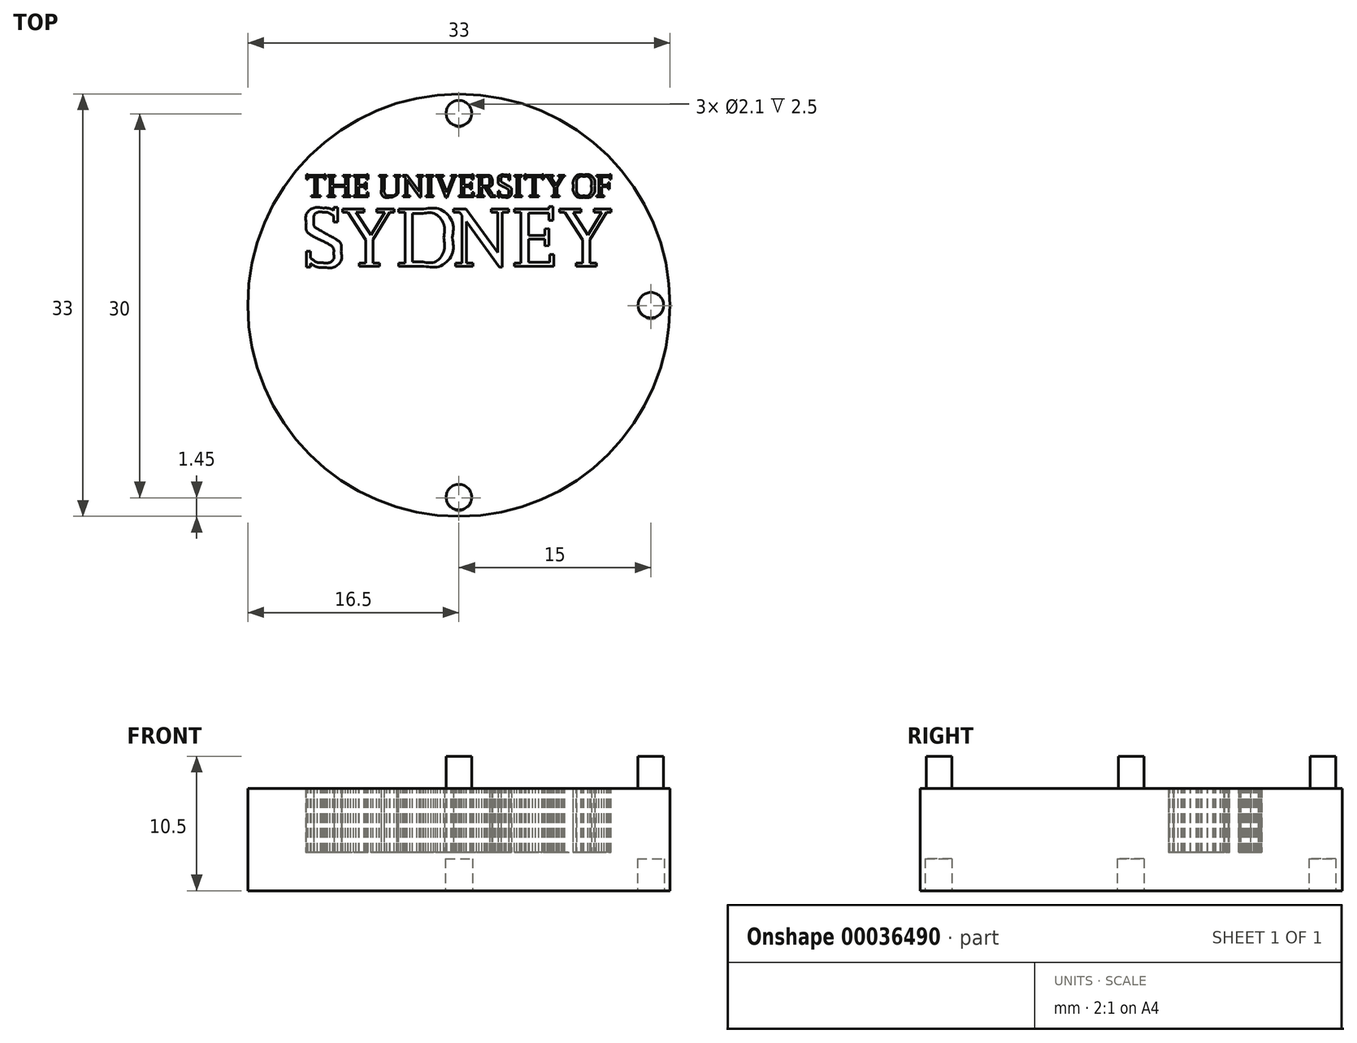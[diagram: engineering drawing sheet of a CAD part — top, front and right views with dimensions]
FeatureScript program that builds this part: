
annotation { "Feature Type Name" : "Feature", "Feature Type Description" : "" }
export const myFeature = defineFeature(function(context is Context, id is Id, definition is map)
    precondition{}
    {
        {
            var Q0;
            Q0=qCreatedBy(makeId("Top.planeOp"),FACE);
            var sketch = newSketch(context, id + "F0", { "sketchPlane" : qUnion([Q0])});
            skCircle(sketch, "E0", {"center": v(0, 0) * mm, "radius": 16.5 * mm});
            skSolve(sketch);
        }
        {
            var Q0;
            Q0=qSketchRegion(id+"F0",true);
            extrude(context, id + "F1", {"entities" : qUnion([Q0]), "depth" : 8 * mm});
        }
        {
            var Q0;
            Q0=makeQuery(id+"F1.opExtrude","CAP_FACE",FACE,{"disambiguationData":[OSD([sQuery(id+"F0.wireOp",EDGE,"E0")])],"isStart":true});
            var sketch = newSketch(context, id + "F2", { "sketchPlane" : qUnion([Q0])});
            skCircle(sketch, "E1", {"center": v(0, 15.05) * mm, "radius": 1.05 * mm});
            skCircle(sketch, "E2.1.0", {"center": v(15, 0.05) * mm, "radius": 1.05 * mm});
            skCircle(sketch, "E2.2.0", {"center": v(0, -14.95) * mm, "radius": 1.05 * mm});
            skPoint(sketch, "E2.center", {"position": v(0, 0.05) * mm});
            skLineSegment(sketch, "E2.anchor1", {"start": v(0, 0.05) * mm, "end": v(0, 15.05) * mm, "construction": true});
            skLineSegment(sketch, "E2.anchor2", {"start": v(0, 0.05) * mm, "end": v(0, -14.95) * mm, "construction": true});
            skSolve(sketch);
        }
        {
            var Q0;
            Q0=qSketchRegion(id+"F2",true);
            extrude(context, id + "F3", {"entities" : qUnion([Q0]), "operationType" : NewBodyOperationType.REMOVE, "oppositeDirection" : true, "depth" : 2.5 * mm});
        }
        {
            var Q0;
            Q0=makeQuery(id+"F1.opExtrude","CAP_FACE",FACE,{"disambiguationData":[OSD([sQuery(id+"F0.wireOp",EDGE,"E0")])],"isStart":false});
            var sketch = newSketch(context, id + "F4", { "sketchPlane" : qUnion([Q0])});
            skCircle(sketch, "E3", {"center": v(0, 15) * mm, "radius": 1 * mm});
            skCircle(sketch, "E4.1.0", {"center": v(15, 0) * mm, "radius": 1 * mm});
            skCircle(sketch, "E4.2.0", {"center": v(0, -15) * mm, "radius": 1 * mm});
            skPoint(sketch, "E4.center", {"position": v(0, 0) * mm});
            skLineSegment(sketch, "E4.anchor1", {"start": v(0, 0) * mm, "end": v(0, 15) * mm, "construction": true});
            skLineSegment(sketch, "E4.anchor2", {"start": v(0, 0) * mm, "end": v(0, -15) * mm, "construction": true});
            skSolve(sketch);
        }
        {
            var Q0;
            Q0=qSketchRegion(id+"F4",true);
            extrude(context, id + "F5", {"entities" : qUnion([Q0]), "operationType" : NewBodyOperationType.ADD, "depth" : 2.5 * mm});
        }
        {
            var Q0;
            Q0=makeQuery(id+"F1.opExtrude","CAP_FACE",FACE,{"disambiguationData":[OSD([sQuery(id+"F0.wireOp",EDGE,"E0")])],"isStart":false});
            var sketch = newSketch(context, id + "F6", { "sketchPlane" : qUnion([Q0])});
            skLineSegment(sketch, "E5", {"start": v(-10.8, 8.46) * mm, "end": v(-11.53, 8.46) * mm});
            skLineSegment(sketch, "E6", {"start": v(-11.53, 8.46) * mm, "end": v(-11.53, 8.56) * mm});
            skLineSegment(sketch, "E7", {"start": v(-11.53, 8.56) * mm, "end": v(-11.28, 8.56) * mm});
            skLineSegment(sketch, "E8", {"start": v(-11.28, 8.56) * mm, "end": v(-11.28, 10.03) * mm});
            skLineSegment(sketch, "E9", {"start": v(-11.28, 10.03) * mm, "end": v(-11.8, 10.03) * mm});
            skLineSegment(sketch, "E10", {"start": v(-11.8, 10.03) * mm, "end": v(-11.8, 9.82) * mm});
            skLineSegment(sketch, "E11", {"start": v(-11.8, 9.82) * mm, "end": v(-11.91, 9.82) * mm});
            skLineSegment(sketch, "E12", {"start": v(-11.91, 9.82) * mm, "end": v(-11.91, 10.23) * mm});
            skLineSegment(sketch, "E13", {"start": v(-11.91, 10.23) * mm, "end": v(-11.8, 10.23) * mm});
            skLineSegment(sketch, "E14", {"start": v(-11.8, 10.23) * mm, "end": v(-11.8, 10.15) * mm});
            skLineSegment(sketch, "E15", {"start": v(-11.8, 10.15) * mm, "end": v(-10.54, 10.15) * mm});
            skLineSegment(sketch, "E16", {"start": v(-10.54, 10.15) * mm, "end": v(-10.54, 10.23) * mm});
            skLineSegment(sketch, "E17", {"start": v(-10.54, 10.23) * mm, "end": v(-10.42, 10.23) * mm});
            skLineSegment(sketch, "E18", {"start": v(-10.42, 10.23) * mm, "end": v(-10.42, 9.82) * mm});
            skLineSegment(sketch, "E19", {"start": v(-10.42, 9.82) * mm, "end": v(-10.54, 9.82) * mm});
            skLineSegment(sketch, "E20", {"start": v(-10.54, 9.82) * mm, "end": v(-10.54, 10.03) * mm});
            skLineSegment(sketch, "E21", {"start": v(-10.54, 10.03) * mm, "end": v(-11.05, 10.03) * mm});
            skLineSegment(sketch, "E22", {"start": v(-11.05, 10.03) * mm, "end": v(-11.05, 8.56) * mm});
            skLineSegment(sketch, "E23", {"start": v(-11.05, 8.56) * mm, "end": v(-10.8, 8.56) * mm});
            skLineSegment(sketch, "E24", {"start": v(-10.8, 8.56) * mm, "end": v(-10.8, 8.46) * mm});
            skLineSegment(sketch, "E25", {"start": v(-8.47, 8.46) * mm, "end": v(-9.08, 8.46) * mm});
            skLineSegment(sketch, "E26", {"start": v(-9.08, 8.46) * mm, "end": v(-9.08, 8.56) * mm});
            skLineSegment(sketch, "E27", {"start": v(-9.08, 8.56) * mm, "end": v(-8.88, 8.56) * mm});
            skLineSegment(sketch, "E28", {"start": v(-8.88, 8.56) * mm, "end": v(-8.88, 9.26) * mm});
            skLineSegment(sketch, "E29", {"start": v(-8.88, 9.26) * mm, "end": v(-9.84, 9.26) * mm});
            skLineSegment(sketch, "E30", {"start": v(-9.84, 9.26) * mm, "end": v(-9.84, 8.56) * mm});
            skLineSegment(sketch, "E31", {"start": v(-9.84, 8.56) * mm, "end": v(-9.65, 8.56) * mm});
            skLineSegment(sketch, "E32", {"start": v(-9.65, 8.56) * mm, "end": v(-9.65, 8.46) * mm});
            skLineSegment(sketch, "E33", {"start": v(-9.65, 8.46) * mm, "end": v(-10.26, 8.46) * mm});
            skLineSegment(sketch, "E34", {"start": v(-10.26, 8.46) * mm, "end": v(-10.26, 8.56) * mm});
            skLineSegment(sketch, "E35", {"start": v(-10.26, 8.56) * mm, "end": v(-10.07, 8.56) * mm});
            skLineSegment(sketch, "E36", {"start": v(-10.07, 8.56) * mm, "end": v(-10.07, 10.06) * mm});
            skLineSegment(sketch, "E37", {"start": v(-10.07, 10.06) * mm, "end": v(-10.26, 10.06) * mm});
            skLineSegment(sketch, "E38", {"start": v(-10.26, 10.06) * mm, "end": v(-10.26, 10.15) * mm});
            skLineSegment(sketch, "E39", {"start": v(-10.26, 10.15) * mm, "end": v(-9.65, 10.15) * mm});
            skLineSegment(sketch, "E40", {"start": v(-9.65, 10.15) * mm, "end": v(-9.65, 10.06) * mm});
            skLineSegment(sketch, "E41", {"start": v(-9.65, 10.06) * mm, "end": v(-9.84, 10.06) * mm});
            skLineSegment(sketch, "E42", {"start": v(-9.84, 10.06) * mm, "end": v(-9.84, 9.38) * mm});
            skLineSegment(sketch, "E43", {"start": v(-9.84, 9.38) * mm, "end": v(-8.88, 9.38) * mm});
            skLineSegment(sketch, "E44", {"start": v(-8.88, 9.38) * mm, "end": v(-8.88, 10.06) * mm});
            skLineSegment(sketch, "E45", {"start": v(-8.88, 10.06) * mm, "end": v(-9.08, 10.06) * mm});
            skLineSegment(sketch, "E46", {"start": v(-9.08, 10.06) * mm, "end": v(-9.08, 10.15) * mm});
            skLineSegment(sketch, "E47", {"start": v(-9.08, 10.15) * mm, "end": v(-8.47, 10.15) * mm});
            skLineSegment(sketch, "E48", {"start": v(-8.47, 10.15) * mm, "end": v(-8.47, 10.06) * mm});
            skLineSegment(sketch, "E49", {"start": v(-8.47, 10.06) * mm, "end": v(-8.66, 10.06) * mm});
            skLineSegment(sketch, "E50", {"start": v(-8.66, 10.06) * mm, "end": v(-8.66, 8.56) * mm});
            skLineSegment(sketch, "E51", {"start": v(-8.66, 8.56) * mm, "end": v(-8.47, 8.56) * mm});
            skLineSegment(sketch, "E52", {"start": v(-8.47, 8.56) * mm, "end": v(-8.47, 8.46) * mm});
            skLineSegment(sketch, "E53", {"start": v(-7.08, 8.46) * mm, "end": v(-8.25, 8.46) * mm});
            skLineSegment(sketch, "E54", {"start": v(-8.25, 8.46) * mm, "end": v(-8.25, 8.56) * mm});
            skLineSegment(sketch, "E55", {"start": v(-8.25, 8.56) * mm, "end": v(-8.06, 8.56) * mm});
            skLineSegment(sketch, "E56", {"start": v(-8.06, 8.56) * mm, "end": v(-8.06, 10.06) * mm});
            skLineSegment(sketch, "E57", {"start": v(-8.06, 10.06) * mm, "end": v(-8.25, 10.06) * mm});
            skLineSegment(sketch, "E58", {"start": v(-8.25, 10.06) * mm, "end": v(-8.25, 10.15) * mm});
            skLineSegment(sketch, "E59", {"start": v(-8.25, 10.15) * mm, "end": v(-7.23, 10.15) * mm});
            skLineSegment(sketch, "E60", {"start": v(-7.23, 10.15) * mm, "end": v(-7.23, 10.23) * mm});
            skLineSegment(sketch, "E61", {"start": v(-7.23, 10.23) * mm, "end": v(-7.1, 10.23) * mm});
            skLineSegment(sketch, "E62", {"start": v(-7.1, 10.23) * mm, "end": v(-7.1, 9.82) * mm});
            skLineSegment(sketch, "E63", {"start": v(-7.1, 9.82) * mm, "end": v(-7.22, 9.82) * mm});
            skLineSegment(sketch, "E64", {"start": v(-7.22, 9.82) * mm, "end": v(-7.22, 10.04) * mm});
            skLineSegment(sketch, "E65", {"start": v(-7.22, 10.04) * mm, "end": v(-7.83, 10.04) * mm});
            skLineSegment(sketch, "E66", {"start": v(-7.83, 10.04) * mm, "end": v(-7.83, 9.38) * mm});
            skLineSegment(sketch, "E67", {"start": v(-7.83, 9.38) * mm, "end": v(-7.35, 9.38) * mm});
            skLineSegment(sketch, "E68", {"start": v(-7.35, 9.38) * mm, "end": v(-7.35, 9.57) * mm});
            skLineSegment(sketch, "E69", {"start": v(-7.35, 9.57) * mm, "end": v(-7.23, 9.57) * mm});
            skLineSegment(sketch, "E70", {"start": v(-7.23, 9.57) * mm, "end": v(-7.23, 9.07) * mm});
            skLineSegment(sketch, "E71", {"start": v(-7.23, 9.07) * mm, "end": v(-7.35, 9.07) * mm});
            skLineSegment(sketch, "E72", {"start": v(-7.35, 9.07) * mm, "end": v(-7.35, 9.26) * mm});
            skLineSegment(sketch, "E73", {"start": v(-7.35, 9.26) * mm, "end": v(-7.83, 9.26) * mm});
            skLineSegment(sketch, "E74", {"start": v(-7.83, 9.26) * mm, "end": v(-7.83, 8.58) * mm});
            skLineSegment(sketch, "E75", {"start": v(-7.83, 8.58) * mm, "end": v(-7.2, 8.58) * mm});
            skLineSegment(sketch, "E76", {"start": v(-7.2, 8.58) * mm, "end": v(-7.2, 8.8) * mm});
            skLineSegment(sketch, "E77", {"start": v(-7.2, 8.8) * mm, "end": v(-7.08, 8.8) * mm});
            skLineSegment(sketch, "E78", {"start": v(-7.08, 8.8) * mm, "end": v(-7.08, 8.46) * mm});
            skLineSegment(sketch, "E79", {"start": v(-4.55, 10.06) * mm, "end": v(-4.74, 10.06) * mm});
            skLineSegment(sketch, "E80", {"start": v(-4.74, 10.06) * mm, "end": v(-4.74, 9.08) * mm});
            skFitSpline(sketch, "E81", {"points": [v(-4.74, 9.08) * mm, v(-4.74, 8.8) * mm, v(-4.84, 8.63) * mm, v(-5.05, 8.52) * mm]});
            skFitSpline(sketch, "E82", {"points": [v(-5.05, 8.52) * mm, v(-5.16, 8.46) * mm, v(-5.28, 8.43) * mm, v(-5.4, 8.43) * mm]});
            skFitSpline(sketch, "E83", {"points": [v(-5.4, 8.43) * mm, v(-5.78, 8.43) * mm, v(-6.06, 8.67) * mm, v(-6.06, 9.01) * mm]});
            skLineSegment(sketch, "E84", {"start": v(-6.06, 9.01) * mm, "end": v(-6.06, 10.06) * mm});
            skLineSegment(sketch, "E85", {"start": v(-6.06, 10.06) * mm, "end": v(-6.25, 10.06) * mm});
            skLineSegment(sketch, "E86", {"start": v(-6.25, 10.06) * mm, "end": v(-6.25, 10.15) * mm});
            skLineSegment(sketch, "E87", {"start": v(-6.25, 10.15) * mm, "end": v(-5.64, 10.15) * mm});
            skLineSegment(sketch, "E88", {"start": v(-5.64, 10.15) * mm, "end": v(-5.64, 10.06) * mm});
            skLineSegment(sketch, "E89", {"start": v(-5.64, 10.06) * mm, "end": v(-5.83, 10.06) * mm});
            skLineSegment(sketch, "E90", {"start": v(-5.83, 10.06) * mm, "end": v(-5.83, 9.09) * mm});
            skFitSpline(sketch, "E91", {"points": [v(-5.83, 9.09) * mm, v(-5.83, 8.78) * mm, v(-5.65, 8.58) * mm, v(-5.36, 8.58) * mm]});
            skFitSpline(sketch, "E92", {"points": [v(-5.36, 8.58) * mm, v(-5.07, 8.58) * mm, v(-4.87, 8.79) * mm, v(-4.87, 9.1) * mm]});
            skLineSegment(sketch, "E93", {"start": v(-4.87, 9.1) * mm, "end": v(-4.87, 10.06) * mm});
            skLineSegment(sketch, "E94", {"start": v(-4.87, 10.06) * mm, "end": v(-5.07, 10.06) * mm});
            skLineSegment(sketch, "E95", {"start": v(-5.07, 10.06) * mm, "end": v(-5.07, 10.15) * mm});
            skLineSegment(sketch, "E96", {"start": v(-5.07, 10.15) * mm, "end": v(-4.55, 10.15) * mm});
            skLineSegment(sketch, "E97", {"start": v(-4.55, 10.15) * mm, "end": v(-4.55, 10.06) * mm});
            skLineSegment(sketch, "E98", {"start": v(-2.97, 8.43) * mm, "end": v(-3.05, 8.43) * mm});
            skLineSegment(sketch, "E99", {"start": v(-3.05, 8.43) * mm, "end": v(-4.03, 9.79) * mm});
            skLineSegment(sketch, "E100", {"start": v(-4.03, 9.79) * mm, "end": v(-4.03, 8.56) * mm});
            skLineSegment(sketch, "E101", {"start": v(-4.03, 8.56) * mm, "end": v(-3.84, 8.56) * mm});
            skLineSegment(sketch, "E102", {"start": v(-3.84, 8.56) * mm, "end": v(-3.84, 8.46) * mm});
            skLineSegment(sketch, "E103", {"start": v(-3.84, 8.46) * mm, "end": v(-4.36, 8.46) * mm});
            skLineSegment(sketch, "E104", {"start": v(-4.36, 8.46) * mm, "end": v(-4.36, 8.56) * mm});
            skLineSegment(sketch, "E105", {"start": v(-4.36, 8.56) * mm, "end": v(-4.16, 8.56) * mm});
            skLineSegment(sketch, "E106", {"start": v(-4.16, 8.56) * mm, "end": v(-4.16, 9.96) * mm});
            skLineSegment(sketch, "E107", {"start": v(-4.16, 9.96) * mm, "end": v(-4.23, 10.06) * mm});
            skLineSegment(sketch, "E108", {"start": v(-4.23, 10.06) * mm, "end": v(-4.4, 10.06) * mm});
            skLineSegment(sketch, "E109", {"start": v(-4.4, 10.06) * mm, "end": v(-4.4, 10.15) * mm});
            skLineSegment(sketch, "E110", {"start": v(-4.4, 10.15) * mm, "end": v(-4.04, 10.15) * mm});
            skLineSegment(sketch, "E111", {"start": v(-4.04, 10.15) * mm, "end": v(-3.1, 8.87) * mm});
            skLineSegment(sketch, "E112", {"start": v(-3.1, 8.87) * mm, "end": v(-3.1, 10.06) * mm});
            skLineSegment(sketch, "E113", {"start": v(-3.1, 10.06) * mm, "end": v(-3.3, 10.06) * mm});
            skLineSegment(sketch, "E114", {"start": v(-3.3, 10.06) * mm, "end": v(-3.3, 10.15) * mm});
            skLineSegment(sketch, "E115", {"start": v(-3.3, 10.15) * mm, "end": v(-2.78, 10.15) * mm});
            skLineSegment(sketch, "E116", {"start": v(-2.78, 10.15) * mm, "end": v(-2.78, 10.06) * mm});
            skLineSegment(sketch, "E117", {"start": v(-2.78, 10.06) * mm, "end": v(-2.97, 10.06) * mm});
            skLineSegment(sketch, "E118", {"start": v(-2.97, 10.06) * mm, "end": v(-2.97, 8.43) * mm});
            skLineSegment(sketch, "E119", {"start": v(-1.98, 8.46) * mm, "end": v(-2.6, 8.46) * mm});
            skLineSegment(sketch, "E120", {"start": v(-2.6, 8.46) * mm, "end": v(-2.6, 8.56) * mm});
            skLineSegment(sketch, "E121", {"start": v(-2.6, 8.56) * mm, "end": v(-2.4, 8.56) * mm});
            skLineSegment(sketch, "E122", {"start": v(-2.4, 8.56) * mm, "end": v(-2.4, 10.06) * mm});
            skLineSegment(sketch, "E123", {"start": v(-2.4, 10.06) * mm, "end": v(-2.6, 10.06) * mm});
            skLineSegment(sketch, "E124", {"start": v(-2.6, 10.06) * mm, "end": v(-2.6, 10.15) * mm});
            skLineSegment(sketch, "E125", {"start": v(-2.6, 10.15) * mm, "end": v(-1.98, 10.15) * mm});
            skLineSegment(sketch, "E126", {"start": v(-1.98, 10.15) * mm, "end": v(-1.98, 10.06) * mm});
            skLineSegment(sketch, "E127", {"start": v(-1.98, 10.06) * mm, "end": v(-2.17, 10.06) * mm});
            skLineSegment(sketch, "E128", {"start": v(-2.17, 10.06) * mm, "end": v(-2.17, 8.56) * mm});
            skLineSegment(sketch, "E129", {"start": v(-2.17, 8.56) * mm, "end": v(-1.98, 8.56) * mm});
            skLineSegment(sketch, "E130", {"start": v(-1.98, 8.56) * mm, "end": v(-1.98, 8.46) * mm});
            skLineSegment(sketch, "E131", {"start": v(-0.94, 8.42) * mm, "end": v(-1.03, 8.42) * mm});
            skLineSegment(sketch, "E132", {"start": v(-1.03, 8.42) * mm, "end": v(-1.68, 10.06) * mm});
            skLineSegment(sketch, "E133", {"start": v(-1.68, 10.06) * mm, "end": v(-1.83, 10.06) * mm});
            skLineSegment(sketch, "E134", {"start": v(-1.83, 10.06) * mm, "end": v(-1.83, 10.15) * mm});
            skLineSegment(sketch, "E135", {"start": v(-1.83, 10.15) * mm, "end": v(-1.2, 10.15) * mm});
            skLineSegment(sketch, "E136", {"start": v(-1.2, 10.15) * mm, "end": v(-1.2, 10.06) * mm});
            skLineSegment(sketch, "E137", {"start": v(-1.2, 10.06) * mm, "end": v(-1.43, 10.06) * mm});
            skLineSegment(sketch, "E138", {"start": v(-1.43, 10.06) * mm, "end": v(-0.94, 8.8) * mm});
            skLineSegment(sketch, "E139", {"start": v(-0.94, 8.8) * mm, "end": v(-0.44, 10.06) * mm});
            skLineSegment(sketch, "E140", {"start": v(-0.44, 10.06) * mm, "end": v(-0.61, 10.06) * mm});
            skLineSegment(sketch, "E141", {"start": v(-0.61, 10.06) * mm, "end": v(-0.61, 10.15) * mm});
            skLineSegment(sketch, "E142", {"start": v(-0.61, 10.15) * mm, "end": v(-0.18, 10.15) * mm});
            skLineSegment(sketch, "E143", {"start": v(-0.18, 10.15) * mm, "end": v(-0.18, 10.06) * mm});
            skLineSegment(sketch, "E144", {"start": v(-0.18, 10.06) * mm, "end": v(-0.3, 10.06) * mm});
            skLineSegment(sketch, "E145", {"start": v(-0.3, 10.06) * mm, "end": v(-0.94, 8.42) * mm});
            skLineSegment(sketch, "E146", {"start": v(1.15, 8.46) * mm, "end": v(-0.02, 8.46) * mm});
            skLineSegment(sketch, "E147", {"start": v(-0.02, 8.46) * mm, "end": v(-0.02, 8.56) * mm});
            skLineSegment(sketch, "E148", {"start": v(-0.02, 8.56) * mm, "end": v(0.17, 8.56) * mm});
            skLineSegment(sketch, "E149", {"start": v(0.17, 8.56) * mm, "end": v(0.17, 10.06) * mm});
            skLineSegment(sketch, "E150", {"start": v(0.17, 10.06) * mm, "end": v(-0.02, 10.06) * mm});
            skLineSegment(sketch, "E151", {"start": v(-0.02, 10.06) * mm, "end": v(-0.02, 10.15) * mm});
            skLineSegment(sketch, "E152", {"start": v(-0.02, 10.15) * mm, "end": v(1, 10.15) * mm});
            skLineSegment(sketch, "E153", {"start": v(1, 10.15) * mm, "end": v(1, 10.23) * mm});
            skLineSegment(sketch, "E154", {"start": v(1, 10.23) * mm, "end": v(1.12, 10.23) * mm});
            skLineSegment(sketch, "E155", {"start": v(1.12, 10.23) * mm, "end": v(1.12, 9.82) * mm});
            skLineSegment(sketch, "E156", {"start": v(1.12, 9.82) * mm, "end": v(1, 9.82) * mm});
            skLineSegment(sketch, "E157", {"start": v(1, 9.82) * mm, "end": v(1, 10.04) * mm});
            skLineSegment(sketch, "E158", {"start": v(1, 10.04) * mm, "end": v(0.4, 10.04) * mm});
            skLineSegment(sketch, "E159", {"start": v(0.4, 10.04) * mm, "end": v(0.4, 9.38) * mm});
            skLineSegment(sketch, "E160", {"start": v(0.4, 9.38) * mm, "end": v(0.88, 9.38) * mm});
            skLineSegment(sketch, "E161", {"start": v(0.88, 9.38) * mm, "end": v(0.88, 9.57) * mm});
            skLineSegment(sketch, "E162", {"start": v(0.88, 9.57) * mm, "end": v(1, 9.57) * mm});
            skLineSegment(sketch, "E163", {"start": v(1, 9.57) * mm, "end": v(1, 9.07) * mm});
            skLineSegment(sketch, "E164", {"start": v(1, 9.07) * mm, "end": v(0.88, 9.07) * mm});
            skLineSegment(sketch, "E165", {"start": v(0.88, 9.07) * mm, "end": v(0.88, 9.26) * mm});
            skLineSegment(sketch, "E166", {"start": v(0.88, 9.26) * mm, "end": v(0.4, 9.26) * mm});
            skLineSegment(sketch, "E167", {"start": v(0.4, 9.26) * mm, "end": v(0.4, 8.58) * mm});
            skLineSegment(sketch, "E168", {"start": v(0.4, 8.58) * mm, "end": v(1.03, 8.58) * mm});
            skLineSegment(sketch, "E169", {"start": v(1.03, 8.58) * mm, "end": v(1.03, 8.8) * mm});
            skLineSegment(sketch, "E170", {"start": v(1.03, 8.8) * mm, "end": v(1.15, 8.8) * mm});
            skLineSegment(sketch, "E171", {"start": v(1.15, 8.8) * mm, "end": v(1.15, 8.46) * mm});
            skLineSegment(sketch, "E172", {"start": v(1.8, 9.34) * mm, "end": v(2.06, 9.34) * mm});
            skFitSpline(sketch, "E173", {"points": [v(2.06, 9.34) * mm, v(2.25, 9.34) * mm, v(2.39, 9.48) * mm, v(2.39, 9.7) * mm]});
            skFitSpline(sketch, "E174", {"points": [v(2.39, 9.7) * mm, v(2.39, 9.91) * mm, v(2.27, 10.04) * mm, v(2.05, 10.04) * mm]});
            skLineSegment(sketch, "E175", {"start": v(2.05, 10.04) * mm, "end": v(1.8, 10.04) * mm});
            skLineSegment(sketch, "E176", {"start": v(1.8, 10.04) * mm, "end": v(1.8, 9.34) * mm});
            skLineSegment(sketch, "E177", {"start": v(2.87, 8.46) * mm, "end": v(2.66, 8.46) * mm});
            skFitSpline(sketch, "E178", {"points": [v(2.66, 8.46) * mm, v(2.5, 8.46) * mm, v(2.48, 8.48) * mm, v(2.4, 8.61) * mm]});
            skLineSegment(sketch, "E179", {"start": v(2.4, 8.61) * mm, "end": v(2, 9.22) * mm});
            skLineSegment(sketch, "E180", {"start": v(2, 9.22) * mm, "end": v(1.8, 9.22) * mm});
            skLineSegment(sketch, "E181", {"start": v(1.8, 9.22) * mm, "end": v(1.8, 8.56) * mm});
            skLineSegment(sketch, "E182", {"start": v(1.8, 8.56) * mm, "end": v(2, 8.56) * mm});
            skLineSegment(sketch, "E183", {"start": v(2, 8.56) * mm, "end": v(2, 8.46) * mm});
            skLineSegment(sketch, "E184", {"start": v(2, 8.46) * mm, "end": v(1.4, 8.46) * mm});
            skLineSegment(sketch, "E185", {"start": v(1.4, 8.46) * mm, "end": v(1.4, 8.56) * mm});
            skLineSegment(sketch, "E186", {"start": v(1.4, 8.56) * mm, "end": v(1.58, 8.56) * mm});
            skLineSegment(sketch, "E187", {"start": v(1.58, 8.56) * mm, "end": v(1.58, 10.06) * mm});
            skLineSegment(sketch, "E188", {"start": v(1.58, 10.06) * mm, "end": v(1.4, 10.06) * mm});
            skLineSegment(sketch, "E189", {"start": v(1.4, 10.06) * mm, "end": v(1.4, 10.15) * mm});
            skLineSegment(sketch, "E190", {"start": v(1.4, 10.15) * mm, "end": v(2.1, 10.15) * mm});
            skFitSpline(sketch, "E191", {"points": [v(2.1, 10.15) * mm, v(2.35, 10.15) * mm, v(2.5, 10.08) * mm, v(2.57, 9.93) * mm]});
            skFitSpline(sketch, "E192", {"points": [v(2.57, 9.93) * mm, v(2.6, 9.86) * mm, v(2.62, 9.78) * mm, v(2.62, 9.7) * mm]});
            skFitSpline(sketch, "E193", {"points": [v(2.62, 9.7) * mm, v(2.62, 9.45) * mm, v(2.48, 9.3) * mm, v(2.24, 9.25) * mm]});
            skLineSegment(sketch, "E194", {"start": v(2.24, 9.25) * mm, "end": v(2.6, 8.69) * mm});
            skFitSpline(sketch, "E195", {"points": [v(2.6, 8.69) * mm, v(2.67, 8.6) * mm, v(2.7, 8.56) * mm, v(2.77, 8.56) * mm]});
            skLineSegment(sketch, "E196", {"start": v(2.77, 8.56) * mm, "end": v(2.87, 8.56) * mm});
            skLineSegment(sketch, "E197", {"start": v(2.87, 8.56) * mm, "end": v(2.87, 8.46) * mm});
            skLineSegment(sketch, "E198", {"start": v(3.2, 8.44) * mm, "end": v(3.08, 8.44) * mm});
            skLineSegment(sketch, "E199", {"start": v(3.08, 8.44) * mm, "end": v(3.08, 8.9) * mm});
            skLineSegment(sketch, "E200", {"start": v(3.08, 8.9) * mm, "end": v(3.2, 8.9) * mm});
            skLineSegment(sketch, "E201", {"start": v(3.2, 8.9) * mm, "end": v(3.2, 8.7) * mm});
            skFitSpline(sketch, "E202", {"points": [v(3.2, 8.7) * mm, v(3.36, 8.6) * mm, v(3.43, 8.57) * mm, v(3.54, 8.57) * mm]});
            skFitSpline(sketch, "E203", {"points": [v(3.54, 8.57) * mm, v(3.74, 8.57) * mm, v(3.88, 8.67) * mm, v(3.88, 8.84) * mm]});
            skFitSpline(sketch, "E204", {"points": [v(3.88, 8.84) * mm, v(3.88, 8.98) * mm, v(3.78, 9.09) * mm, v(3.5, 9.23) * mm]});
            skFitSpline(sketch, "E205", {"points": [v(3.5, 9.23) * mm, v(3.18, 9.4) * mm, v(3.07, 9.53) * mm, v(3.07, 9.74) * mm]});
            skFitSpline(sketch, "E206", {"points": [v(3.07, 9.74) * mm, v(3.07, 10) * mm, v(3.29, 10.19) * mm, v(3.58, 10.19) * mm]});
            skFitSpline(sketch, "E207", {"points": [v(3.58, 10.19) * mm, v(3.7, 10.19) * mm, v(3.8, 10.16) * mm, v(3.88, 10.11) * mm]});
            skLineSegment(sketch, "E208", {"start": v(3.88, 10.11) * mm, "end": v(3.88, 10.2) * mm});
            skLineSegment(sketch, "E209", {"start": v(3.88, 10.2) * mm, "end": v(4, 10.2) * mm});
            skLineSegment(sketch, "E210", {"start": v(4, 10.2) * mm, "end": v(4, 9.77) * mm});
            skLineSegment(sketch, "E211", {"start": v(4, 9.77) * mm, "end": v(3.88, 9.77) * mm});
            skLineSegment(sketch, "E212", {"start": v(3.88, 9.77) * mm, "end": v(3.88, 9.95) * mm});
            skFitSpline(sketch, "E213", {"points": [v(3.88, 9.95) * mm, v(3.75, 10.04) * mm, v(3.69, 10.06) * mm, v(3.59, 10.06) * mm]});
            skFitSpline(sketch, "E214", {"points": [v(3.59, 10.06) * mm, v(3.41, 10.06) * mm, v(3.3, 9.96) * mm, v(3.3, 9.8) * mm]});
            skFitSpline(sketch, "E215", {"points": [v(3.3, 9.8) * mm, v(3.3, 9.67) * mm, v(3.37, 9.6) * mm, v(3.7, 9.4) * mm]});
            skFitSpline(sketch, "E216", {"points": [v(3.7, 9.4) * mm, v(4.01, 9.22) * mm, v(4.1, 9.11) * mm, v(4.1, 8.9) * mm]});
            skFitSpline(sketch, "E217", {"points": [v(4.1, 8.9) * mm, v(4.1, 8.63) * mm, v(3.89, 8.43) * mm, v(3.6, 8.43) * mm]});
            skFitSpline(sketch, "E218", {"points": [v(3.6, 8.43) * mm, v(3.43, 8.43) * mm, v(3.33, 8.46) * mm, v(3.2, 8.54) * mm]});
            skLineSegment(sketch, "E219", {"start": v(3.2, 8.54) * mm, "end": v(3.2, 8.44) * mm});
            skLineSegment(sketch, "E220", {"start": v(4.95, 8.46) * mm, "end": v(4.34, 8.46) * mm});
            skLineSegment(sketch, "E221", {"start": v(4.34, 8.46) * mm, "end": v(4.34, 8.56) * mm});
            skLineSegment(sketch, "E222", {"start": v(4.34, 8.56) * mm, "end": v(4.53, 8.56) * mm});
            skLineSegment(sketch, "E223", {"start": v(4.53, 8.56) * mm, "end": v(4.53, 10.06) * mm});
            skLineSegment(sketch, "E224", {"start": v(4.53, 10.06) * mm, "end": v(4.34, 10.06) * mm});
            skLineSegment(sketch, "E225", {"start": v(4.34, 10.06) * mm, "end": v(4.34, 10.15) * mm});
            skLineSegment(sketch, "E226", {"start": v(4.34, 10.15) * mm, "end": v(4.95, 10.15) * mm});
            skLineSegment(sketch, "E227", {"start": v(4.95, 10.15) * mm, "end": v(4.95, 10.06) * mm});
            skLineSegment(sketch, "E228", {"start": v(4.95, 10.06) * mm, "end": v(4.76, 10.06) * mm});
            skLineSegment(sketch, "E229", {"start": v(4.76, 10.06) * mm, "end": v(4.76, 8.56) * mm});
            skLineSegment(sketch, "E230", {"start": v(4.76, 8.56) * mm, "end": v(4.95, 8.56) * mm});
            skLineSegment(sketch, "E231", {"start": v(4.95, 8.56) * mm, "end": v(4.95, 8.46) * mm});
            skLineSegment(sketch, "E232", {"start": v(6.24, 8.46) * mm, "end": v(5.5, 8.46) * mm});
            skLineSegment(sketch, "E233", {"start": v(5.5, 8.46) * mm, "end": v(5.5, 8.56) * mm});
            skLineSegment(sketch, "E234", {"start": v(5.5, 8.56) * mm, "end": v(5.75, 8.56) * mm});
            skLineSegment(sketch, "E235", {"start": v(5.75, 8.56) * mm, "end": v(5.75, 10.03) * mm});
            skLineSegment(sketch, "E236", {"start": v(5.75, 10.03) * mm, "end": v(5.24, 10.03) * mm});
            skLineSegment(sketch, "E237", {"start": v(5.24, 10.03) * mm, "end": v(5.24, 9.82) * mm});
            skLineSegment(sketch, "E238", {"start": v(5.24, 9.82) * mm, "end": v(5.12, 9.82) * mm});
            skLineSegment(sketch, "E239", {"start": v(5.12, 9.82) * mm, "end": v(5.12, 10.23) * mm});
            skLineSegment(sketch, "E240", {"start": v(5.12, 10.23) * mm, "end": v(5.24, 10.23) * mm});
            skLineSegment(sketch, "E241", {"start": v(5.24, 10.23) * mm, "end": v(5.24, 10.15) * mm});
            skLineSegment(sketch, "E242", {"start": v(5.24, 10.15) * mm, "end": v(6.5, 10.15) * mm});
            skLineSegment(sketch, "E243", {"start": v(6.5, 10.15) * mm, "end": v(6.5, 10.23) * mm});
            skLineSegment(sketch, "E244", {"start": v(6.5, 10.23) * mm, "end": v(6.62, 10.23) * mm});
            skLineSegment(sketch, "E245", {"start": v(6.62, 10.23) * mm, "end": v(6.62, 9.82) * mm});
            skLineSegment(sketch, "E246", {"start": v(6.62, 9.82) * mm, "end": v(6.5, 9.82) * mm});
            skLineSegment(sketch, "E247", {"start": v(6.5, 9.82) * mm, "end": v(6.5, 10.03) * mm});
            skLineSegment(sketch, "E248", {"start": v(6.5, 10.03) * mm, "end": v(5.98, 10.03) * mm});
            skLineSegment(sketch, "E249", {"start": v(5.98, 10.03) * mm, "end": v(5.98, 8.56) * mm});
            skLineSegment(sketch, "E250", {"start": v(5.98, 8.56) * mm, "end": v(6.24, 8.56) * mm});
            skLineSegment(sketch, "E251", {"start": v(6.24, 8.56) * mm, "end": v(6.24, 8.46) * mm});
            skLineSegment(sketch, "E252", {"start": v(7.86, 8.46) * mm, "end": v(7.25, 8.46) * mm});
            skLineSegment(sketch, "E253", {"start": v(7.25, 8.46) * mm, "end": v(7.25, 8.56) * mm});
            skLineSegment(sketch, "E254", {"start": v(7.25, 8.56) * mm, "end": v(7.44, 8.56) * mm});
            skLineSegment(sketch, "E255", {"start": v(7.44, 8.56) * mm, "end": v(7.44, 9.24) * mm});
            skLineSegment(sketch, "E256", {"start": v(7.44, 9.24) * mm, "end": v(6.9, 10.06) * mm});
            skLineSegment(sketch, "E257", {"start": v(6.9, 10.06) * mm, "end": v(6.76, 10.06) * mm});
            skLineSegment(sketch, "E258", {"start": v(6.76, 10.06) * mm, "end": v(6.76, 10.15) * mm});
            skLineSegment(sketch, "E259", {"start": v(6.76, 10.15) * mm, "end": v(7.4, 10.15) * mm});
            skLineSegment(sketch, "E260", {"start": v(7.4, 10.15) * mm, "end": v(7.4, 10.06) * mm});
            skLineSegment(sketch, "E261", {"start": v(7.4, 10.06) * mm, "end": v(7.16, 10.06) * mm});
            skLineSegment(sketch, "E262", {"start": v(7.16, 10.06) * mm, "end": v(7.6, 9.39) * mm});
            skLineSegment(sketch, "E263", {"start": v(7.6, 9.39) * mm, "end": v(8, 10.06) * mm});
            skLineSegment(sketch, "E264", {"start": v(8, 10.06) * mm, "end": v(7.77, 10.06) * mm});
            skLineSegment(sketch, "E265", {"start": v(7.77, 10.06) * mm, "end": v(7.77, 10.15) * mm});
            skLineSegment(sketch, "E266", {"start": v(7.77, 10.15) * mm, "end": v(8.29, 10.15) * mm});
            skLineSegment(sketch, "E267", {"start": v(8.29, 10.15) * mm, "end": v(8.29, 10.06) * mm});
            skLineSegment(sketch, "E268", {"start": v(8.29, 10.06) * mm, "end": v(8.15, 10.06) * mm});
            skLineSegment(sketch, "E269", {"start": v(8.15, 10.06) * mm, "end": v(7.66, 9.26) * mm});
            skLineSegment(sketch, "E270", {"start": v(7.66, 9.26) * mm, "end": v(7.66, 8.56) * mm});
            skLineSegment(sketch, "E271", {"start": v(7.66, 8.56) * mm, "end": v(7.86, 8.56) * mm});
            skLineSegment(sketch, "E272", {"start": v(7.86, 8.56) * mm, "end": v(7.86, 8.46) * mm});
            skFitSpline(sketch, "E273", {"points": [v(9.2, 9.3) * mm, v(9.2, 8.87) * mm, v(9.44, 8.56) * mm, v(9.78, 8.56) * mm]});
            skFitSpline(sketch, "E274", {"points": [v(9.78, 8.56) * mm, v(10.1, 8.56) * mm, v(10.34, 8.88) * mm, v(10.34, 9.3) * mm]});
            skFitSpline(sketch, "E275", {"points": [v(10.34, 9.3) * mm, v(10.34, 9.74) * mm, v(10.1, 10.05) * mm, v(9.78, 10.05) * mm]});
            skFitSpline(sketch, "E276", {"points": [v(9.78, 10.05) * mm, v(9.44, 10.05) * mm, v(9.2, 9.74) * mm, v(9.2, 9.3) * mm]});
            skFitSpline(sketch, "E277", {"points": [v(8.95, 9.3) * mm, v(8.95, 9.79) * mm, v(9.32, 10.19) * mm, v(9.78, 10.19) * mm]});
            skFitSpline(sketch, "E278", {"points": [v(9.78, 10.19) * mm, v(10.22, 10.19) * mm, v(10.6, 9.79) * mm, v(10.6, 9.3) * mm]});
            skFitSpline(sketch, "E279", {"points": [v(10.6, 9.3) * mm, v(10.6, 8.83) * mm, v(10.22, 8.43) * mm, v(9.78, 8.43) * mm]});
            skFitSpline(sketch, "E280", {"points": [v(9.78, 8.43) * mm, v(9.33, 8.43) * mm, v(8.95, 8.83) * mm, v(8.95, 9.3) * mm]});
            skLineSegment(sketch, "E281", {"start": v(11.37, 8.46) * mm, "end": v(10.76, 8.46) * mm});
            skLineSegment(sketch, "E282", {"start": v(10.76, 8.46) * mm, "end": v(10.76, 8.56) * mm});
            skLineSegment(sketch, "E283", {"start": v(10.76, 8.56) * mm, "end": v(10.95, 8.56) * mm});
            skLineSegment(sketch, "E284", {"start": v(10.95, 8.56) * mm, "end": v(10.95, 10.06) * mm});
            skLineSegment(sketch, "E285", {"start": v(10.95, 10.06) * mm, "end": v(10.76, 10.06) * mm});
            skLineSegment(sketch, "E286", {"start": v(10.76, 10.06) * mm, "end": v(10.76, 10.15) * mm});
            skLineSegment(sketch, "E287", {"start": v(10.76, 10.15) * mm, "end": v(11.78, 10.15) * mm});
            skLineSegment(sketch, "E288", {"start": v(11.78, 10.15) * mm, "end": v(11.78, 10.23) * mm});
            skLineSegment(sketch, "E289", {"start": v(11.78, 10.23) * mm, "end": v(11.9, 10.23) * mm});
            skLineSegment(sketch, "E290", {"start": v(11.9, 10.23) * mm, "end": v(11.9, 9.82) * mm});
            skLineSegment(sketch, "E291", {"start": v(11.9, 9.82) * mm, "end": v(11.78, 9.82) * mm});
            skLineSegment(sketch, "E292", {"start": v(11.78, 9.82) * mm, "end": v(11.78, 10.04) * mm});
            skLineSegment(sketch, "E293", {"start": v(11.78, 10.04) * mm, "end": v(11.17, 10.04) * mm});
            skLineSegment(sketch, "E294", {"start": v(11.17, 10.04) * mm, "end": v(11.17, 9.38) * mm});
            skLineSegment(sketch, "E295", {"start": v(11.17, 9.38) * mm, "end": v(11.66, 9.38) * mm});
            skLineSegment(sketch, "E296", {"start": v(11.66, 9.38) * mm, "end": v(11.66, 9.57) * mm});
            skLineSegment(sketch, "E297", {"start": v(11.66, 9.57) * mm, "end": v(11.78, 9.57) * mm});
            skLineSegment(sketch, "E298", {"start": v(11.78, 9.57) * mm, "end": v(11.78, 9.07) * mm});
            skLineSegment(sketch, "E299", {"start": v(11.78, 9.07) * mm, "end": v(11.66, 9.07) * mm});
            skLineSegment(sketch, "E300", {"start": v(11.66, 9.07) * mm, "end": v(11.66, 9.26) * mm});
            skLineSegment(sketch, "E301", {"start": v(11.66, 9.26) * mm, "end": v(11.17, 9.26) * mm});
            skLineSegment(sketch, "E302", {"start": v(11.17, 9.26) * mm, "end": v(11.17, 8.56) * mm});
            skLineSegment(sketch, "E303", {"start": v(11.17, 8.56) * mm, "end": v(11.37, 8.56) * mm});
            skLineSegment(sketch, "E304", {"start": v(11.37, 8.56) * mm, "end": v(11.37, 8.46) * mm});
            skLineSegment(sketch, "E305", {"start": v(-11.6, 2.98) * mm, "end": v(-11.91, 2.98) * mm});
            skLineSegment(sketch, "E306", {"start": v(-11.91, 2.98) * mm, "end": v(-11.91, 4.2) * mm});
            skLineSegment(sketch, "E307", {"start": v(-11.91, 4.2) * mm, "end": v(-11.6, 4.2) * mm});
            skLineSegment(sketch, "E308", {"start": v(-11.6, 4.2) * mm, "end": v(-11.6, 3.67) * mm});
            skFitSpline(sketch, "E309", {"points": [v(-11.6, 3.67) * mm, v(-11.18, 3.39) * mm, v(-11, 3.32) * mm, v(-10.7, 3.32) * mm]});
            skFitSpline(sketch, "E310", {"points": [v(-10.7, 3.32) * mm, v(-10.16, 3.32) * mm, v(-9.8, 3.6) * mm, v(-9.8, 4.03) * mm]});
            skFitSpline(sketch, "E311", {"points": [v(-9.8, 4.03) * mm, v(-9.8, 4.42) * mm, v(-10.06, 4.7) * mm, v(-10.8, 5.08) * mm]});
            skFitSpline(sketch, "E312", {"points": [v(-10.8, 5.08) * mm, v(-11.64, 5.52) * mm, v(-11.93, 5.86) * mm, v(-11.93, 6.42) * mm]});
            skFitSpline(sketch, "E313", {"points": [v(-11.93, 6.42) * mm, v(-11.93, 7.09) * mm, v(-11.36, 7.59) * mm, v(-10.6, 7.59) * mm]});
            skFitSpline(sketch, "E314", {"points": [v(-10.6, 7.59) * mm, v(-10.26, 7.59) * mm, v(-10.01, 7.53) * mm, v(-9.8, 7.4) * mm]});
            skLineSegment(sketch, "E315", {"start": v(-9.8, 7.4) * mm, "end": v(-9.8, 7.64) * mm});
            skLineSegment(sketch, "E316", {"start": v(-9.8, 7.64) * mm, "end": v(-9.49, 7.64) * mm});
            skLineSegment(sketch, "E317", {"start": v(-9.49, 7.64) * mm, "end": v(-9.49, 6.49) * mm});
            skLineSegment(sketch, "E318", {"start": v(-9.49, 6.49) * mm, "end": v(-9.8, 6.49) * mm});
            skLineSegment(sketch, "E319", {"start": v(-9.8, 6.49) * mm, "end": v(-9.8, 6.97) * mm});
            skFitSpline(sketch, "E320", {"points": [v(-9.8, 6.97) * mm, v(-10.14, 7.2) * mm, v(-10.31, 7.27) * mm, v(-10.58, 7.27) * mm]});
            skFitSpline(sketch, "E321", {"points": [v(-10.58, 7.27) * mm, v(-11.04, 7.27) * mm, v(-11.34, 6.99) * mm, v(-11.34, 6.57) * mm]});
            skFitSpline(sketch, "E322", {"points": [v(-11.34, 6.57) * mm, v(-11.34, 6.22) * mm, v(-11.14, 6.03) * mm, v(-10.3, 5.54) * mm]});
            skFitSpline(sketch, "E323", {"points": [v(-10.3, 5.54) * mm, v(-9.45, 5.05) * mm, v(-9.2, 4.75) * mm, v(-9.2, 4.2) * mm]});
            skFitSpline(sketch, "E324", {"points": [v(-9.2, 4.2) * mm, v(-9.2, 3.5) * mm, v(-9.8, 2.96) * mm, v(-10.55, 2.96) * mm]});
            skFitSpline(sketch, "E325", {"points": [v(-10.55, 2.96) * mm, v(-10.98, 2.96) * mm, v(-11.26, 3.05) * mm, v(-11.6, 3.26) * mm]});
            skLineSegment(sketch, "E326", {"start": v(-11.6, 3.26) * mm, "end": v(-11.6, 2.98) * mm});
            skLineSegment(sketch, "E327", {"start": v(-6.2, 3.05) * mm, "end": v(-7.8, 3.05) * mm});
            skLineSegment(sketch, "E328", {"start": v(-7.8, 3.05) * mm, "end": v(-7.8, 3.3) * mm});
            skLineSegment(sketch, "E329", {"start": v(-7.8, 3.3) * mm, "end": v(-7.3, 3.3) * mm});
            skLineSegment(sketch, "E330", {"start": v(-7.3, 3.3) * mm, "end": v(-7.3, 5.1) * mm});
            skLineSegment(sketch, "E331", {"start": v(-7.3, 5.1) * mm, "end": v(-8.7, 7.26) * mm});
            skLineSegment(sketch, "E332", {"start": v(-8.7, 7.26) * mm, "end": v(-9.09, 7.26) * mm});
            skLineSegment(sketch, "E333", {"start": v(-9.09, 7.26) * mm, "end": v(-9.09, 7.5) * mm});
            skLineSegment(sketch, "E334", {"start": v(-9.09, 7.5) * mm, "end": v(-7.42, 7.5) * mm});
            skLineSegment(sketch, "E335", {"start": v(-7.42, 7.5) * mm, "end": v(-7.42, 7.26) * mm});
            skLineSegment(sketch, "E336", {"start": v(-7.42, 7.26) * mm, "end": v(-8.03, 7.26) * mm});
            skLineSegment(sketch, "E337", {"start": v(-8.03, 7.26) * mm, "end": v(-6.87, 5.48) * mm});
            skLineSegment(sketch, "E338", {"start": v(-6.87, 5.48) * mm, "end": v(-5.8, 7.26) * mm});
            skLineSegment(sketch, "E339", {"start": v(-5.8, 7.26) * mm, "end": v(-6.41, 7.26) * mm});
            skLineSegment(sketch, "E340", {"start": v(-6.41, 7.26) * mm, "end": v(-6.41, 7.5) * mm});
            skLineSegment(sketch, "E341", {"start": v(-6.41, 7.5) * mm, "end": v(-5.06, 7.5) * mm});
            skLineSegment(sketch, "E342", {"start": v(-5.06, 7.5) * mm, "end": v(-5.06, 7.26) * mm});
            skLineSegment(sketch, "E343", {"start": v(-5.06, 7.26) * mm, "end": v(-5.41, 7.26) * mm});
            skLineSegment(sketch, "E344", {"start": v(-5.41, 7.26) * mm, "end": v(-6.7, 5.14) * mm});
            skLineSegment(sketch, "E345", {"start": v(-6.7, 5.14) * mm, "end": v(-6.7, 3.3) * mm});
            skLineSegment(sketch, "E346", {"start": v(-6.7, 3.3) * mm, "end": v(-6.2, 3.3) * mm});
            skLineSegment(sketch, "E347", {"start": v(-6.2, 3.3) * mm, "end": v(-6.2, 3.05) * mm});
            skLineSegment(sketch, "E348", {"start": v(-3.62, 3.38) * mm, "end": v(-2.81, 3.38) * mm});
            skFitSpline(sketch, "E349", {"points": [v(-2.81, 3.38) * mm, v(-1.89, 3.38) * mm, v(-1.18, 4.2) * mm, v(-1.19, 5.27) * mm]});
            skFitSpline(sketch, "E350", {"points": [v(-1.19, 5.27) * mm, v(-1.19, 6.32) * mm, v(-1.9, 7.16) * mm, v(-2.8, 7.16) * mm]});
            skLineSegment(sketch, "E351", {"start": v(-2.8, 7.16) * mm, "end": v(-3.62, 7.16) * mm});
            skLineSegment(sketch, "E352", {"start": v(-3.62, 7.16) * mm, "end": v(-3.62, 3.38) * mm});
            skLineSegment(sketch, "E353", {"start": v(-4.72, 3.05) * mm, "end": v(-4.72, 3.3) * mm});
            skLineSegment(sketch, "E354", {"start": v(-4.72, 3.3) * mm, "end": v(-4.22, 3.3) * mm});
            skLineSegment(sketch, "E355", {"start": v(-4.22, 3.3) * mm, "end": v(-4.22, 7.26) * mm});
            skLineSegment(sketch, "E356", {"start": v(-4.22, 7.26) * mm, "end": v(-4.72, 7.26) * mm});
            skLineSegment(sketch, "E357", {"start": v(-4.72, 7.26) * mm, "end": v(-4.72, 7.5) * mm});
            skLineSegment(sketch, "E358", {"start": v(-4.72, 7.5) * mm, "end": v(-2.73, 7.5) * mm});
            skFitSpline(sketch, "E359", {"points": [v(-2.73, 7.5) * mm, v(-1.51, 7.5) * mm, v(-0.52, 6.5) * mm, v(-0.52, 5.28) * mm]});
            skFitSpline(sketch, "E360", {"points": [v(-0.52, 5.28) * mm, v(-0.52, 4.03) * mm, v(-1.5, 3.05) * mm, v(-2.74, 3.05) * mm]});
            skLineSegment(sketch, "E361", {"start": v(-2.74, 3.05) * mm, "end": v(-4.72, 3.05) * mm});
            skLineSegment(sketch, "E362", {"start": v(3.38, 2.97) * mm, "end": v(3.17, 2.97) * mm});
            skLineSegment(sketch, "E363", {"start": v(3.17, 2.97) * mm, "end": v(0.57, 6.54) * mm});
            skLineSegment(sketch, "E364", {"start": v(0.57, 6.54) * mm, "end": v(0.57, 3.3) * mm});
            skLineSegment(sketch, "E365", {"start": v(0.57, 3.3) * mm, "end": v(1.09, 3.3) * mm});
            skLineSegment(sketch, "E366", {"start": v(1.09, 3.3) * mm, "end": v(1.09, 3.05) * mm});
            skLineSegment(sketch, "E367", {"start": v(1.09, 3.05) * mm, "end": v(-0.28, 3.05) * mm});
            skLineSegment(sketch, "E368", {"start": v(-0.28, 3.05) * mm, "end": v(-0.28, 3.3) * mm});
            skLineSegment(sketch, "E369", {"start": v(-0.28, 3.3) * mm, "end": v(0.24, 3.3) * mm});
            skLineSegment(sketch, "E370", {"start": v(0.24, 3.3) * mm, "end": v(0.24, 7) * mm});
            skLineSegment(sketch, "E371", {"start": v(0.24, 7) * mm, "end": v(0.05, 7.26) * mm});
            skLineSegment(sketch, "E372", {"start": v(0.05, 7.26) * mm, "end": v(-0.41, 7.26) * mm});
            skLineSegment(sketch, "E373", {"start": v(-0.41, 7.26) * mm, "end": v(-0.41, 7.5) * mm});
            skLineSegment(sketch, "E374", {"start": v(-0.41, 7.5) * mm, "end": v(0.57, 7.5) * mm});
            skLineSegment(sketch, "E375", {"start": v(0.57, 7.5) * mm, "end": v(3.04, 4.11) * mm});
            skLineSegment(sketch, "E376", {"start": v(3.04, 4.11) * mm, "end": v(3.04, 7.26) * mm});
            skLineSegment(sketch, "E377", {"start": v(3.04, 7.26) * mm, "end": v(2.53, 7.26) * mm});
            skLineSegment(sketch, "E378", {"start": v(2.53, 7.26) * mm, "end": v(2.53, 7.5) * mm});
            skLineSegment(sketch, "E379", {"start": v(2.53, 7.5) * mm, "end": v(3.89, 7.5) * mm});
            skLineSegment(sketch, "E380", {"start": v(3.89, 7.5) * mm, "end": v(3.89, 7.26) * mm});
            skLineSegment(sketch, "E381", {"start": v(3.89, 7.26) * mm, "end": v(3.38, 7.26) * mm});
            skLineSegment(sketch, "E382", {"start": v(3.38, 7.26) * mm, "end": v(3.38, 2.97) * mm});
            skLineSegment(sketch, "E383", {"start": v(7.42, 3.05) * mm, "end": v(4.34, 3.05) * mm});
            skLineSegment(sketch, "E384", {"start": v(4.34, 3.05) * mm, "end": v(4.34, 3.3) * mm});
            skLineSegment(sketch, "E385", {"start": v(4.34, 3.3) * mm, "end": v(4.85, 3.3) * mm});
            skLineSegment(sketch, "E386", {"start": v(4.85, 3.3) * mm, "end": v(4.85, 7.26) * mm});
            skLineSegment(sketch, "E387", {"start": v(4.85, 7.26) * mm, "end": v(4.34, 7.26) * mm});
            skLineSegment(sketch, "E388", {"start": v(4.34, 7.26) * mm, "end": v(4.34, 7.5) * mm});
            skLineSegment(sketch, "E389", {"start": v(4.34, 7.5) * mm, "end": v(7.04, 7.5) * mm});
            skLineSegment(sketch, "E390", {"start": v(7.04, 7.5) * mm, "end": v(7.04, 7.7) * mm});
            skLineSegment(sketch, "E391", {"start": v(7.04, 7.7) * mm, "end": v(7.35, 7.7) * mm});
            skLineSegment(sketch, "E392", {"start": v(7.35, 7.7) * mm, "end": v(7.35, 6.62) * mm});
            skLineSegment(sketch, "E393", {"start": v(7.35, 6.62) * mm, "end": v(7.05, 6.62) * mm});
            skLineSegment(sketch, "E394", {"start": v(7.05, 6.62) * mm, "end": v(7.05, 7.2) * mm});
            skLineSegment(sketch, "E395", {"start": v(7.05, 7.2) * mm, "end": v(5.45, 7.2) * mm});
            skLineSegment(sketch, "E396", {"start": v(5.45, 7.2) * mm, "end": v(5.45, 5.46) * mm});
            skLineSegment(sketch, "E397", {"start": v(5.45, 5.46) * mm, "end": v(6.72, 5.46) * mm});
            skLineSegment(sketch, "E398", {"start": v(6.72, 5.46) * mm, "end": v(6.72, 5.97) * mm});
            skLineSegment(sketch, "E399", {"start": v(6.72, 5.97) * mm, "end": v(7.03, 5.98) * mm});
            skLineSegment(sketch, "E400", {"start": v(7.03, 5.98) * mm, "end": v(7.03, 4.65) * mm});
            skLineSegment(sketch, "E401", {"start": v(7.03, 4.65) * mm, "end": v(6.72, 4.64) * mm});
            skLineSegment(sketch, "E402", {"start": v(6.72, 4.64) * mm, "end": v(6.72, 5.16) * mm});
            skLineSegment(sketch, "E403", {"start": v(6.72, 5.16) * mm, "end": v(5.45, 5.16) * mm});
            skLineSegment(sketch, "E404", {"start": v(5.45, 5.16) * mm, "end": v(5.45, 3.35) * mm});
            skLineSegment(sketch, "E405", {"start": v(5.45, 3.35) * mm, "end": v(7.1, 3.35) * mm});
            skLineSegment(sketch, "E406", {"start": v(7.1, 3.35) * mm, "end": v(7.1, 3.94) * mm});
            skLineSegment(sketch, "E407", {"start": v(7.1, 3.94) * mm, "end": v(7.42, 3.94) * mm});
            skLineSegment(sketch, "E408", {"start": v(7.42, 3.94) * mm, "end": v(7.42, 3.05) * mm});
            skLineSegment(sketch, "E409", {"start": v(10.76, 3.05) * mm, "end": v(9.16, 3.05) * mm});
            skLineSegment(sketch, "E410", {"start": v(9.16, 3.05) * mm, "end": v(9.16, 3.3) * mm});
            skLineSegment(sketch, "E411", {"start": v(9.16, 3.3) * mm, "end": v(9.66, 3.3) * mm});
            skLineSegment(sketch, "E412", {"start": v(9.66, 3.3) * mm, "end": v(9.66, 5.1) * mm});
            skLineSegment(sketch, "E413", {"start": v(9.66, 5.1) * mm, "end": v(8.26, 7.26) * mm});
            skLineSegment(sketch, "E414", {"start": v(8.26, 7.26) * mm, "end": v(7.87, 7.26) * mm});
            skLineSegment(sketch, "E415", {"start": v(7.87, 7.26) * mm, "end": v(7.87, 7.5) * mm});
            skLineSegment(sketch, "E416", {"start": v(7.87, 7.5) * mm, "end": v(9.54, 7.5) * mm});
            skLineSegment(sketch, "E417", {"start": v(9.54, 7.5) * mm, "end": v(9.54, 7.26) * mm});
            skLineSegment(sketch, "E418", {"start": v(9.54, 7.26) * mm, "end": v(8.93, 7.26) * mm});
            skLineSegment(sketch, "E419", {"start": v(8.93, 7.26) * mm, "end": v(10.09, 5.48) * mm});
            skLineSegment(sketch, "E420", {"start": v(10.09, 5.48) * mm, "end": v(11.16, 7.26) * mm});
            skLineSegment(sketch, "E421", {"start": v(11.16, 7.26) * mm, "end": v(10.55, 7.26) * mm});
            skLineSegment(sketch, "E422", {"start": v(10.55, 7.26) * mm, "end": v(10.55, 7.5) * mm});
            skLineSegment(sketch, "E423", {"start": v(10.55, 7.5) * mm, "end": v(11.9, 7.5) * mm});
            skLineSegment(sketch, "E424", {"start": v(11.9, 7.5) * mm, "end": v(11.9, 7.26) * mm});
            skLineSegment(sketch, "E425", {"start": v(11.9, 7.26) * mm, "end": v(11.55, 7.26) * mm});
            skLineSegment(sketch, "E426", {"start": v(11.55, 7.26) * mm, "end": v(10.25, 5.14) * mm});
            skLineSegment(sketch, "E427", {"start": v(10.25, 5.14) * mm, "end": v(10.25, 3.3) * mm});
            skLineSegment(sketch, "E428", {"start": v(10.25, 3.3) * mm, "end": v(10.76, 3.3) * mm});
            skLineSegment(sketch, "E429", {"start": v(10.76, 3.3) * mm, "end": v(10.76, 3.05) * mm});
            skSolve(sketch);
        }
        {
            var Q0;
            Q0 = qSketchRegion(id + "F6", true);
            extrude(context, id + "F7", {"entities" : qUnion([Q0]), "operationType" : NewBodyOperationType.REMOVE, "oppositeDirection" : true, "depth" : 5 * mm});
        }
    });
